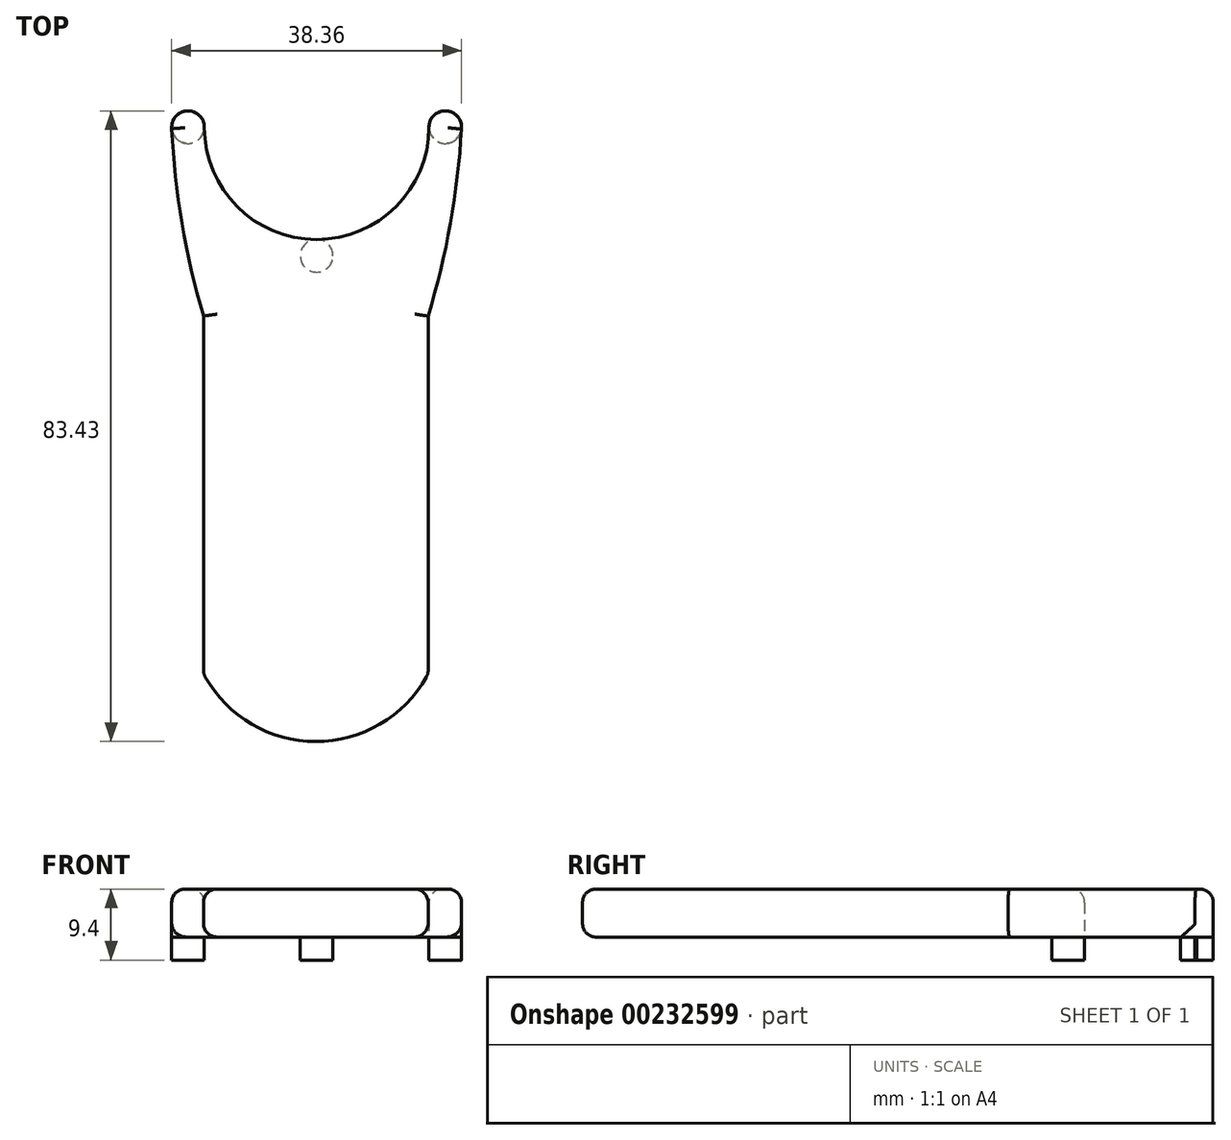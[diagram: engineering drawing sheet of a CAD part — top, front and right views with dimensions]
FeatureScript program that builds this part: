
annotation { "Feature Type Name" : "Feature", "Feature Type Description" : "" }
export const myFeature = defineFeature(function(context is Context, id is Id, definition is map)
    precondition{}
    {
        {
            var Q0;
            Q0=qCreatedBy(makeId("Top.planeOp"),FACE);
            var sketch = newSketch(context, id + "F0", { "sketchPlane" : qUnion([Q0])});
            skCircle(sketch, "E0", {"center": v(-17.02, 0) * mm, "radius": 2.16 * mm});
            skArc(sketch, "E1", {"start": v(-14.96, -72.28) * mm, "mid": v(-0.1, -81.27) * mm, "end": v(14.75, -72.28) * mm});
            skCircle(sketch, "E2", {"center": v(0, -17.02) * mm, "radius": 2.16 * mm});
            skCircle(sketch, "E3", {"center": v(17.02, 0) * mm, "radius": 2.16 * mm});
            skArc(sketch, "E4", {"start": v(-14.86, 0) * mm, "mid": v(0, -14.86) * mm, "end": v(14.86, 0) * mm});
            skLineSegment(sketch, "E5.trimOffspring", {"start": v(-14.96, -24.98) * mm, "end": v(-14.96, -72.28) * mm});
            skLineSegment(sketch, "E6.trimOffspring", {"start": v(14.75, -24.98) * mm, "end": v(14.75, -72.28) * mm});
            skArc(sketch, "E7", {"start": v(-19.18, 0) * mm, "mid": v(-17.83, -12.62) * mm, "end": v(-14.96, -24.98) * mm});
            skArc(sketch, "E8.trimOffspring", {"start": v(14.75, -24.98) * mm, "mid": v(17.71, -12.62) * mm, "end": v(19.18, 0) * mm});
            skSolve(sketch);
        }
        {
            var Q0;
            Q0 = qSketchRegion(id + "F0", true);
            extrude(context, id + "F1", {"entities" : qUnion([Q0]), "depth" : 6.35 * mm});
        }
        {
            var Q0;
            {var subQ0=sQuery(id+"F0.wireOp",EDGE,"E0");var subQ1=makeQuery(id+"F0.imprint","INTERSECT",VERTEX,{"derivedFrom":[subQ0,sQuery(id+"F0.wireOp",EDGE,"E4")]});Q0=makeQuery(id+"F0.imprint","IMPRINT",FACE,{"disambiguationData":[TD([[makeQuery(id+"F0.imprint","IMPRINT",EDGE,{"disambiguationData":[TD([[subQ1,-1.0]])],"derivedFrom":subQ0}),1.0]])]});}
            var Q1;
            Q1=makeQuery(id+"F0.imprint","IMPRINT",FACE,{"disambiguationData":[TD([[makeQuery(id+"F0.imprint","IMPRINT",EDGE,{"derivedFrom":sQuery(id+"F0.wireOp",EDGE,"E2")}),1.0]])]});
            var Q2;
            {var subQ0=sQuery(id+"F0.wireOp",EDGE,"E3");var subQ1=makeQuery(id+"F0.imprint","INTERSECT",VERTEX,{"derivedFrom":[subQ0,sQuery(id+"F0.wireOp",EDGE,"E4")]});Q2=makeQuery(id+"F0.imprint","IMPRINT",FACE,{"disambiguationData":[TD([[makeQuery(id+"F0.imprint","IMPRINT",EDGE,{"disambiguationData":[TD([[subQ1,1.0]])],"derivedFrom":subQ0}),1.0]])]});}
            var Q3;
            Q3=sQuery(id+"F0.wireOp",EDGE,"E3");
            var Q4;
            Q4=sQuery(id+"F0.wireOp",EDGE,"E0");
            var Q5;
            Q5=sQuery(id+"F0.wireOp",EDGE,"E2");
            extrude(context, id + "F2", {"entities" : qUnion([Q0, Q1, Q2]), "surfaceEntities" : qUnion([Q3, Q4, Q5]), "oppositeDirection" : true, "depth" : 3.05 * mm});
        }
        {
            var Q0;
            Q0=makeQuery(id+"F1.opExtrude","CAP_EDGE",EDGE,{"disambiguationData":[OSD([sQuery(id+"F0.wireOp",EDGE,"E5.trimOffspring")])],"isStart":false});
            var Q1;
            Q1=makeQuery(id+"F1.opExtrude","CAP_EDGE",EDGE,{"disambiguationData":[OSD([sQuery(id+"F0.wireOp",EDGE,"E6.trimOffspring")])],"isStart":false});
            var Q2;
            Q2=makeQuery(id+"F1.opExtrude","SWEPT_EDGE",EDGE,{"disambiguationData":[OSD([sQuery(id+"F0.wireOp",EDGE,"E1"),sQuery(id+"F0.wireOp",EDGE,"E5.trimOffspring")])]});
            var Q3;
            Q3=makeQuery(id+"F1.opExtrude","SWEPT_EDGE",EDGE,{"disambiguationData":[OSD([sQuery(id+"F0.wireOp",EDGE,"E1"),sQuery(id+"F0.wireOp",EDGE,"E6.trimOffspring")])]});
            var Q4;
            Q4=makeQuery(id+"F1.opExtrude","CAP_EDGE",EDGE,{"disambiguationData":[OSD([sQuery(id+"F0.wireOp",EDGE,"E1")])],"isStart":false});
            var Q5;
            Q5=makeQuery(id+"F1.opExtrude","CAP_EDGE",EDGE,{"disambiguationData":[OSD([sQuery(id+"F0.wireOp",EDGE,"E5.trimOffspring")])],"isStart":true});
            var Q6;
            Q6=makeQuery(id+"F1.opExtrude","CAP_EDGE",EDGE,{"disambiguationData":[OSD([sQuery(id+"F0.wireOp",EDGE,"E1")])],"isStart":true});
            var Q7;
            Q7=makeQuery(id+"F1.opExtrude","CAP_EDGE",EDGE,{"disambiguationData":[OSD([sQuery(id+"F0.wireOp",EDGE,"E6.trimOffspring")])],"isStart":true});
            var Q8;
            Q8=makeQuery(id+"F1.opExtrude","CAP_EDGE",EDGE,{"disambiguationData":[OSD([sQuery(id+"F0.wireOp",EDGE,"E8.trimOffspring")])],"isStart":true});
            var Q9;
            Q9=makeQuery(id+"F1.opExtrude","CAP_EDGE",EDGE,{"disambiguationData":[OSD([sQuery(id+"F0.wireOp",EDGE,"E8.trimOffspring")])],"isStart":false});
            var Q10;
            Q10=makeQuery(id+"F1.opExtrude","CAP_EDGE",EDGE,{"disambiguationData":[OSD([sQuery(id+"F0.wireOp",EDGE,"E7")])],"isStart":false});
            var Q11;
            Q11=makeQuery(id+"F1.opExtrude","CAP_EDGE",EDGE,{"disambiguationData":[OSD([sQuery(id+"F0.wireOp",EDGE,"E7")])],"isStart":true});
            var Q12;
            Q12=makeQuery(id+"F1.opExtrude","CAP_EDGE",EDGE,{"disambiguationData":[OSD([sQuery(id+"F0.wireOp",EDGE,"E0")])],"isStart":false});
            fillet(context, id + "F3", {"entities" : qUnion([Q0, Q1, Q2, Q3, Q4, Q5, Q6, Q7, Q8, Q9, Q10, Q11, Q12]), "radius" : 1.78 * mm, "tangentPropagation" : true, "allowEdgeOverflow" : false});
        }
    });
